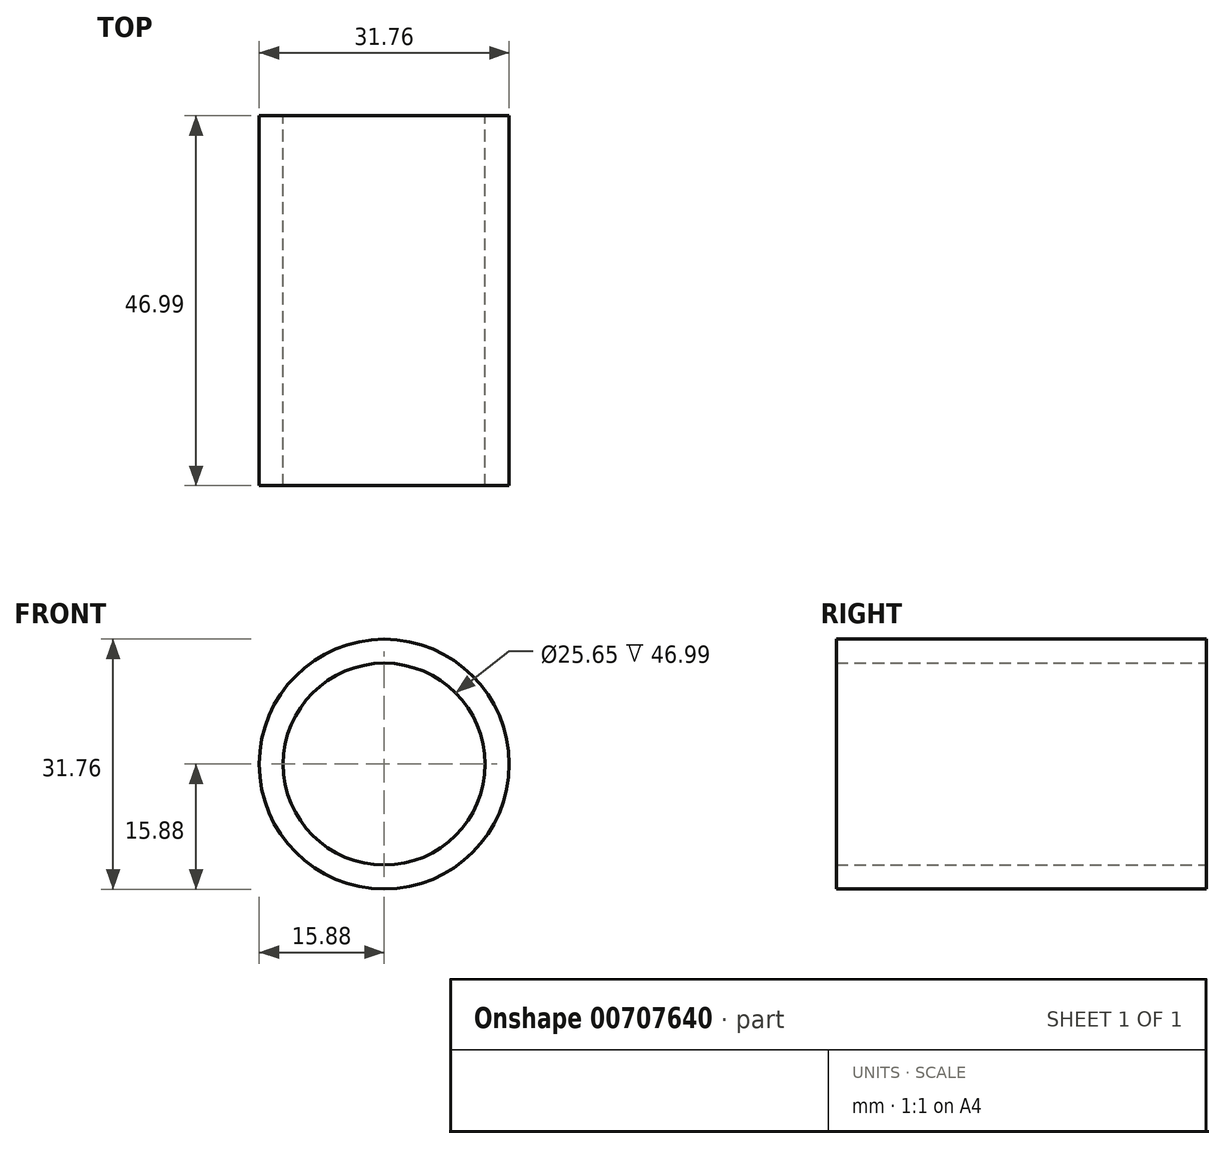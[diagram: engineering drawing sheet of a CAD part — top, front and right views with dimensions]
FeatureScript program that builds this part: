
annotation { "Feature Type Name" : "Feature", "Feature Type Description" : "" }
export const myFeature = defineFeature(function(context is Context, id is Id, definition is map)
    precondition{}
    {
        {
            var Q0;
            Q0=qCreatedBy(makeId("Front.planeOp"),FACE);
            var sketch = newSketch(context, id + "F0", { "sketchPlane" : qUnion([Q0])});
            skCircle(sketch, "E0", {"center": v(0, 0) * mm, "radius": 15.88 * mm});
            skCircle(sketch, "E1", {"center": v(0, 0) * mm, "radius": 12.83 * mm});
            skSolve(sketch);
        }
        {
            var Q0;
            Q0=qSketchRegion(id+"F0",true);
            extrude(context, id + "F1", {"entities" : qUnion([Q0]), "depth" : 47 * mm, "offsetDistance" : 25.4 * mm});
        }
    });
